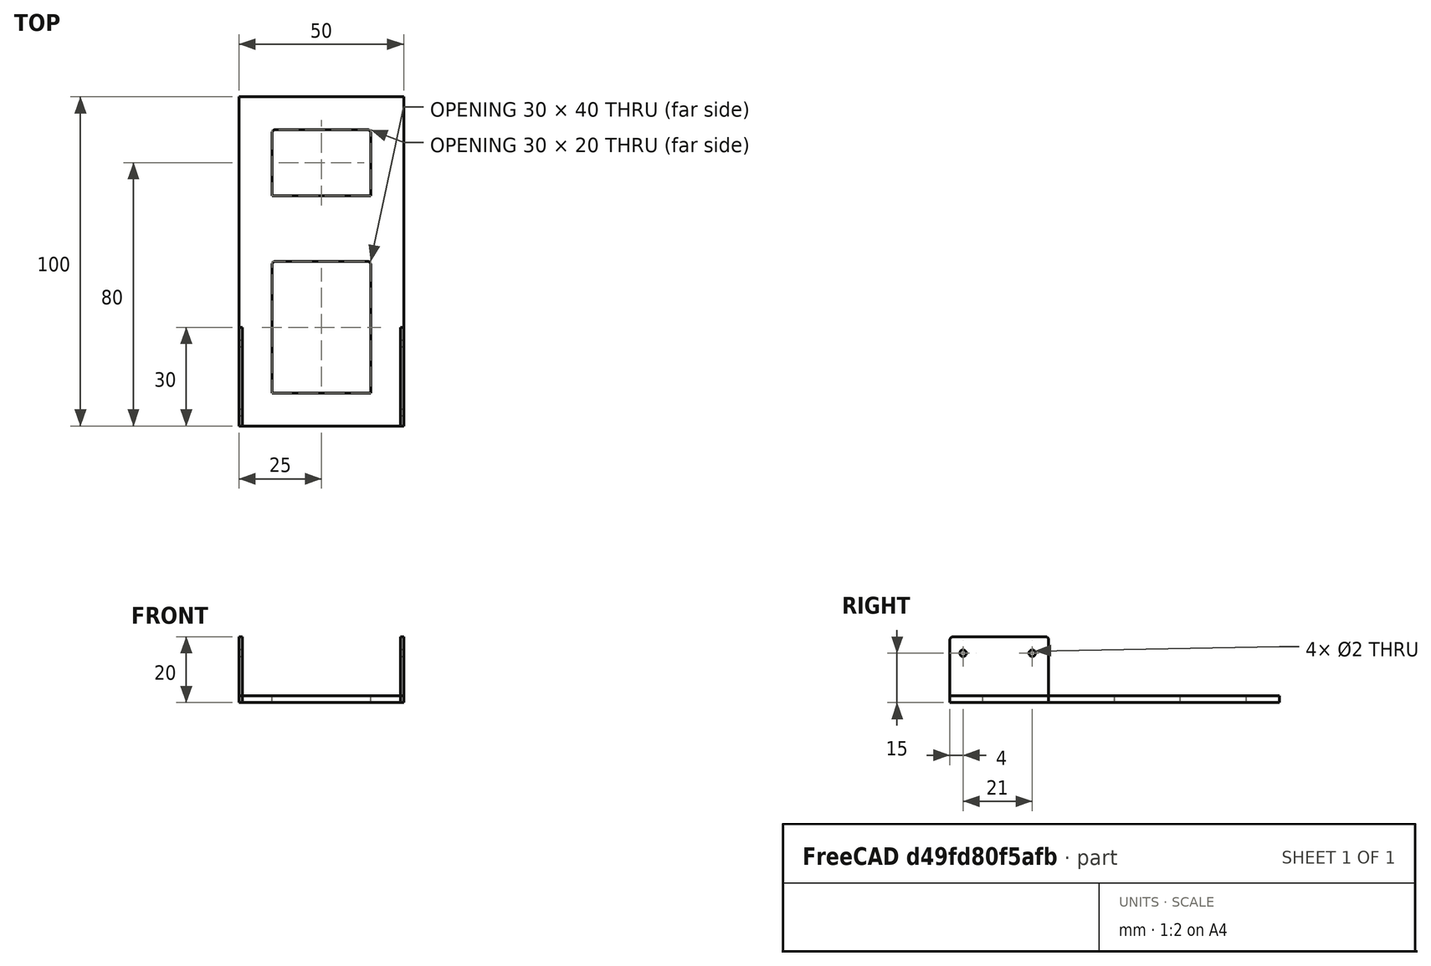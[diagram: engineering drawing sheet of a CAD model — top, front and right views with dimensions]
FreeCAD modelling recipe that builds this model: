
FCSTD DOCUMENT  (FreeCAD 0.18.4R)
Label: EjercicioVideo12
License: All rights reserved
LicenseURL: http://en.wikipedia.org/wiki/All_rights_reserved
objects: Part::Box×5, Part::Fillet×3, Part::Cut×2, Part::Cylinder×2, Part::MultiFuse×1, Part::FeaturePython×1, Part::Fuse×1
note: 15 computed .brp shape members not serialized (recipe doc carries the construction recipe); baked Part::Feature solids carry a one-line shape summary decoded from their .brp

FEATURE [Part::Box] Box  label="Cubo"
  AttacherType = Attacher::AttachEngine3D
  Height = 2
  Length = 50
  Width = 100
FEATURE [Part::Box] Box001  label="Cubo001"
  AttacherType = Attacher::AttachEngine3D
  Height = 10
  Length = 30
  Placement = pos=(10,10,0) rot=(0,0,1;0rad)
  Width = 40
FEATURE [Part::Box] Box002  label="Cubo002"
  AttacherType = Attacher::AttachEngine3D
  Height = 10
  Length = 30
  Placement = pos=(10,70,0) rot=(0,0,1;0rad)
  Width = 20
FEATURE [Part::MultiFuse] Fusion
  Shapes = -> [Box002,Box001]
FEATURE [Part::Cut] Cut
  Base = -> Box
  Tool = -> Fusion
FEATURE [Part::Box] Box003  label="Cubo003"
  AttacherType = Attacher::AttachEngine3D
  Height = 20
  Length = 1
  Width = 30
FEATURE [Part::Cylinder] Cylinder  label="Cilindro"
  Angle = 360
  AttacherType = Attacher::AttachEngine3D
  Height = 52
  Placement = pos=(0,4,15) rot=(0,1,0;1.5708rad)
  Radius = 1
FEATURE [Part::Box] Box004  label="Cubo004"
  AttacherType = Attacher::AttachEngine3D
  Height = 20
  Length = 1
  Placement = pos=(49,0,0) rot=(0,0,1;0rad)
  Width = 30
FEATURE [Part::Cylinder] Cylinder001  label="Cilindro001"
  Angle = 360
  AttacherType = Attacher::AttachEngine3D
  Height = 52
  Placement = pos=(0,25,15) rot=(0,1,0;1.5708rad)
  Radius = 1
FEATURE [Part::FeaturePython] BooleanFragments  # WARN: FeaturePython — macro-defined, semantics opaque (R4)
  Mode = 0
  Objects = -> [Cylinder,Cylinder001]
  Tolerance = 0
FEATURE [Part::Fuse] Fusion001
  Base = -> Box003
  Refine = true
  Tool = -> Box004
FEATURE [Part::Cut] Cut001
  Base = -> Fusion001
  Refine = true
  Tool = -> BooleanFragments
FEATURE [Part::Fillet] Fillet
  Base = -> Cut001
  Edges = 4 edges r=1: [Edge9,Edge10,Edge27,Edge28]
FEATURE [Part::Fillet] Fillet001
  Base = -> Cut
  Edges = 2 edges r=1: [Edge32,Edge36]
FEATURE [Part::Fillet] Fillet002
  Base = -> Fillet001
  Edges = 2 edges r=1: [Edge16,Edge34]
